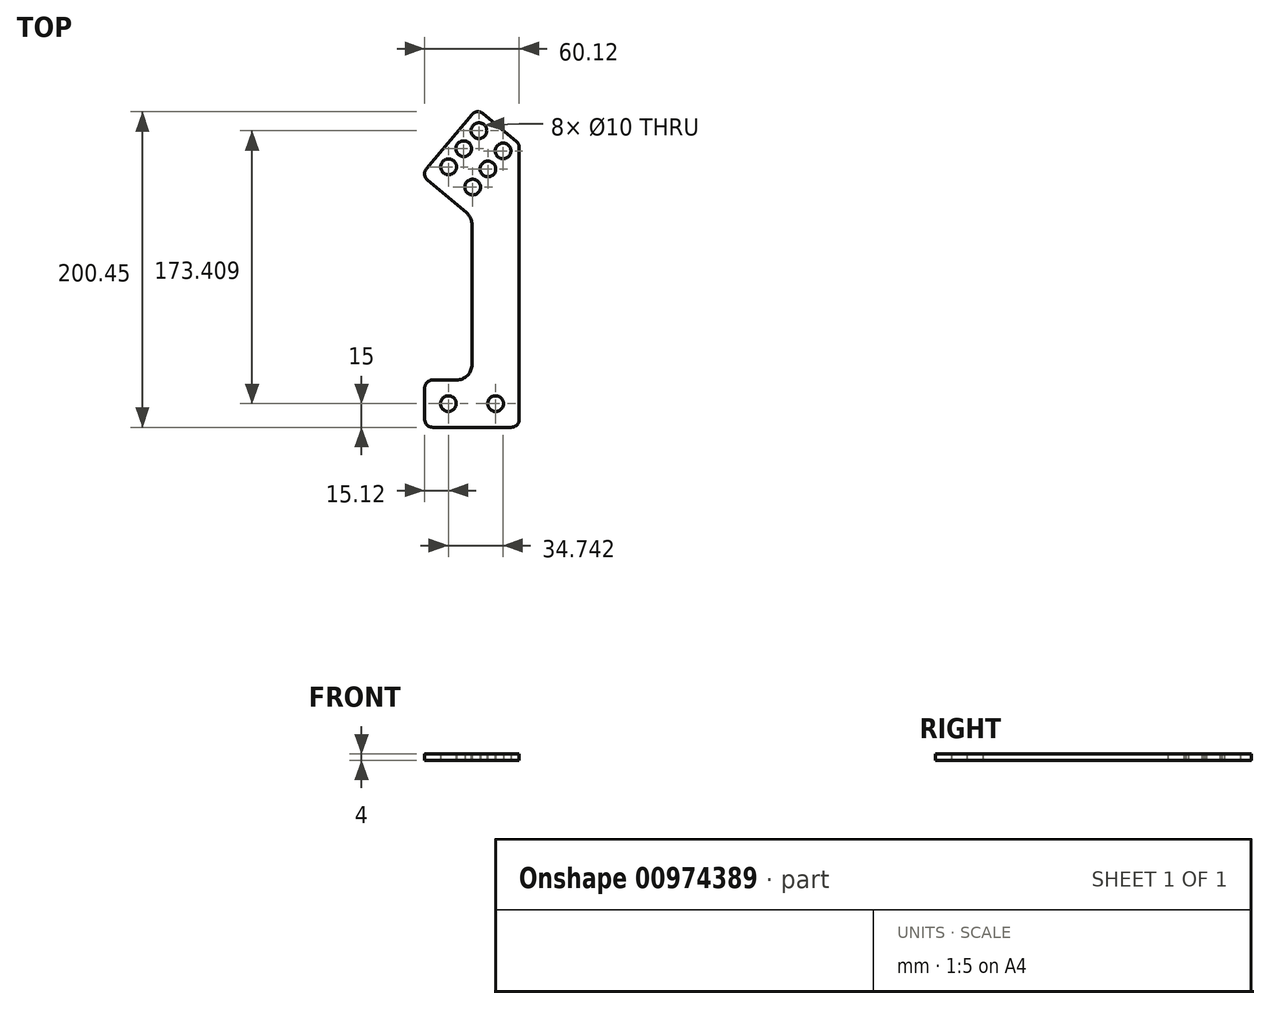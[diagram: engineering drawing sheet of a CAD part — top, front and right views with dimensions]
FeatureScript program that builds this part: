
annotation { "Feature Type Name" : "Feature", "Feature Type Description" : "" }
export const myFeature = defineFeature(function(context is Context, id is Id, definition is map)
    precondition{}
    {
        {
            var Q0;
            Q0=qCreatedBy(makeId("Top.planeOp"),FACE);
            var sketch = newSketch(context, id + "F0", { "sketchPlane" : qUnion([Q0])});
            skLineSegment(sketch, "E0", {"start": v(0, 0) * mm, "end": v(0, 180) * mm});
            skLineSegment(sketch, "E1", {"start": v(0, 180) * mm, "end": v(-26.81, 202.5) * mm});
            skLineSegment(sketch, "E2", {"start": v(-26.81, 202.5) * mm, "end": v(-62.16, 160.37) * mm});
            skLineSegment(sketch, "E3", {"start": v(-62.16, 160.37) * mm, "end": v(-30, 133.38) * mm});
            skLineSegment(sketch, "E4", {"start": v(-30, 133.38) * mm, "end": v(-30, 30) * mm});
            skLineSegment(sketch, "E5", {"start": v(-30, 30) * mm, "end": v(-60, 30) * mm});
            skLineSegment(sketch, "E6", {"start": v(-60, 30) * mm, "end": v(-60, 0) * mm});
            skLineSegment(sketch, "E7", {"start": v(-60, 0) * mm, "end": v(0, 0) * mm});
            skLineSegment(sketch, "E8", {"start": v(-19.15, 196.07) * mm, "end": v(-54.5, 153.94) * mm, "construction": true});
            skLineSegment(sketch, "E9", {"start": v(-3.83, 183.21) * mm, "end": v(-39.18, 141.08) * mm, "construction": true});
            skLineSegment(sketch, "E10", {"start": v(-44.86, 165.43) * mm, "end": v(-29.54, 152.57) * mm, "construction": true});
            skLineSegment(sketch, "E11", {"start": v(-25.58, 188.4) * mm, "end": v(-10.26, 175.55) * mm, "construction": true});
            skLineSegment(sketch, "E12", {"start": v(-35.22, 176.92) * mm, "end": v(-19.9, 164.06) * mm, "construction": true});
            skCircle(sketch, "E13", {"center": v(-25.58, 188.4) * mm, "radius": 5 * mm});
            skCircle(sketch, "E14", {"center": v(-10.26, 175.55) * mm, "radius": 5 * mm});
            skCircle(sketch, "E15", {"center": v(-19.9, 164.06) * mm, "radius": 5 * mm});
            skCircle(sketch, "E16", {"center": v(-35.22, 176.92) * mm, "radius": 5 * mm});
            skCircle(sketch, "E17", {"center": v(-44.86, 165.43) * mm, "radius": 5 * mm});
            skCircle(sketch, "E18", {"center": v(-29.54, 152.57) * mm, "radius": 5 * mm});
            skLineSegment(sketch, "E19", {"start": v(-60, 15) * mm, "end": v(0, 15) * mm, "construction": true});
            skPoint(sketch, "E19.endSnap0", {"position": v(-60, 15) * mm});
            skCircle(sketch, "E20", {"center": v(-45, 15) * mm, "radius": 5 * mm});
            skCircle(sketch, "E21", {"center": v(-15, 15) * mm, "radius": 5 * mm});
            skSolve(sketch);
        }
        {
            var Q0;
            Q0 = qSketchRegion(id + "F0", true);
            extrude(context, id + "F1", {"entities" : qUnion([Q0]), "depth" : 4 * mm, "offsetDistance" : 25 * mm});
        }
        {
            var Q0;
            Q0=makeQuery(id+"F1.opExtrude","SWEPT_EDGE",EDGE,{"disambiguationData":[OSD([sQuery(id+"F0.wireOp",EDGE,"E2"),sQuery(id+"F0.wireOp",EDGE,"E3")])]});
            var Q1;
            Q1=makeQuery(id+"F1.opExtrude","SWEPT_EDGE",EDGE,{"disambiguationData":[OSD([sQuery(id+"F0.wireOp",EDGE,"E1"),sQuery(id+"F0.wireOp",EDGE,"E2")])]});
            var Q2;
            Q2=makeQuery(id+"F1.opExtrude","SWEPT_EDGE",EDGE,{"disambiguationData":[OSD([sQuery(id+"F0.wireOp",EDGE,"E0"),sQuery(id+"F0.wireOp",EDGE,"E1")])]});
            var Q3;
            Q3=makeQuery(id+"F1.opExtrude","SWEPT_EDGE",EDGE,{"disambiguationData":[OSD([sQuery(id+"F0.wireOp",EDGE,"E0"),sQuery(id+"F0.wireOp",EDGE,"E7")])]});
            var Q4;
            Q4=makeQuery(id+"F1.opExtrude","SWEPT_EDGE",EDGE,{"disambiguationData":[OSD([sQuery(id+"F0.wireOp",EDGE,"E6"),sQuery(id+"F0.wireOp",EDGE,"E7")])]});
            var Q5;
            Q5=makeQuery(id+"F1.opExtrude","SWEPT_EDGE",EDGE,{"disambiguationData":[OSD([sQuery(id+"F0.wireOp",EDGE,"E5"),sQuery(id+"F0.wireOp",EDGE,"E6")])]});
            fillet(context, id + "F2", {"entities" : qUnion([Q0, Q1, Q2, Q3, Q4, Q5]), "radius" : 5 * mm, "tangentPropagation" : true, "allowEdgeOverflow" : false});
        }
        {
            var Q0;
            Q0=makeQuery(id+"F1.opExtrude","SWEPT_EDGE",EDGE,{"disambiguationData":[OSD([sQuery(id+"F0.wireOp",EDGE,"E4"),sQuery(id+"F0.wireOp",EDGE,"E5")])]});
            var Q1;
            Q1=makeQuery(id+"F1.opExtrude","SWEPT_EDGE",EDGE,{"disambiguationData":[OSD([sQuery(id+"F0.wireOp",EDGE,"E3"),sQuery(id+"F0.wireOp",EDGE,"E4")])]});
            fillet(context, id + "F3", {"entities" : qUnion([Q0, Q1]), "radius" : 10 * mm, "tangentPropagation" : true, "allowEdgeOverflow" : false});
        }
    });
